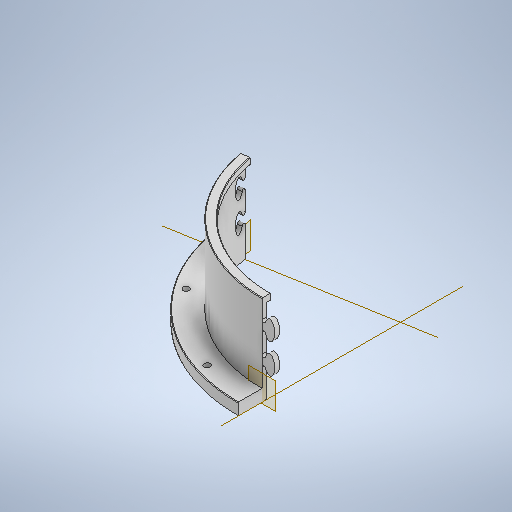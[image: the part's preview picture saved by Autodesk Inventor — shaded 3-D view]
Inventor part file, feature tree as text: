
AUTODESK INVENTOR PART (.ipt)
format: ipt  version: 2025 (Build 290162000, 162)  size: 441,856 bytes
history: native  units: in
note: dims shown in document units (in); Inventor stores cm internally (conversion verified against a paired STEP export)
features: other x15, sketch x7, extrude x7, chamfer x2, plane x1
ambient origin geometry x8: Origin, YZ Plane, XZ Plane, XY Plane, X Axis, Y Axis, Z Axis, Center Point
bodies: Solid1 (feature_tree)
feature tree (32):
  other  "Table"
  other  "Cylinder Segment - 01"
  other  "Cylinder Segment - 02"
  other  "Cylinder Segment - 03"
  other  "Cylinder Segment - 04"
  other  "Cylinder Segment - 05"
  other  "Cylinder Segment - 06"
  other  "Cylinder Segment - 07"
  other  "Cylinder Segment - 08"
  other  "Cylinder Segment - 09"
  other  "Cylinder Segment - 10"
  other  "Cylinder Segment - Face"
  sketch  "Sketch1"  dims[d5=0.0in d7=0.0in]
  extrude  "Extrusion1"  TaperAngle=0.0deg  [1 undecoded]
  extrude  "Extrusion2"  Depth=0.0787in TaperAngle=45.0deg
  extrude  "Extrusion7"  Depth=10.0394in
  chamfer  "Chamfer1"  Distance=3.937in Angle=360.0deg
  chamfer  "Chamfer2"  Distance=0.3937in
  extrude  "Extrusion8"  TaperAngle=0.0deg  [1 undecoded]
  extrude  "Quadrant Cut"  Depth=0.3937in TaperAngle=0.0deg
  other  "Bm Plane"
  plane  "Work Plane2"
  extrude  "Extrusion10"  TaperAngle=0.0deg  [1 undecoded]
  extrude  "Extrusion11"  [1 undecoded]
  sketch  "Sketch2"  dims[d25=0.0787in d26=45.0deg d27=10.0394in]
  sketch  "Sketch3"  dims[d28=0.1969in d29=3.937in d31=360.0deg d33=0.3937in d34=0.0in]
  sketch  "Sketch Circular Pattern1"  dims[d18=0.0in d22=0.0787in d23=45.0deg]
  sketch  "Sketch5"  dims[d48=0.5497in d49=0.0in d50=0.0in]
  other  "Work Axis1"
  other  "Work Axis2"
  sketch  "Sketch6"  dims[d51=0.315in d52=0.1575in d53=0.1181in d54=0.1772in d56=0.3937in d57=0.0in]
  sketch  "Sketch7"  dims[d58=0.1614in d59=0.3189in d60=0.1772in d61=0.122in d62=0.0039in d63=0.0039in d64=0.0in d65=0.0in]
note: 4 required parameter values undecoded (feature->parameter linkage not recoverable at this tier; creation-order binding heuristic only, values carry confidence <= 0.55)
